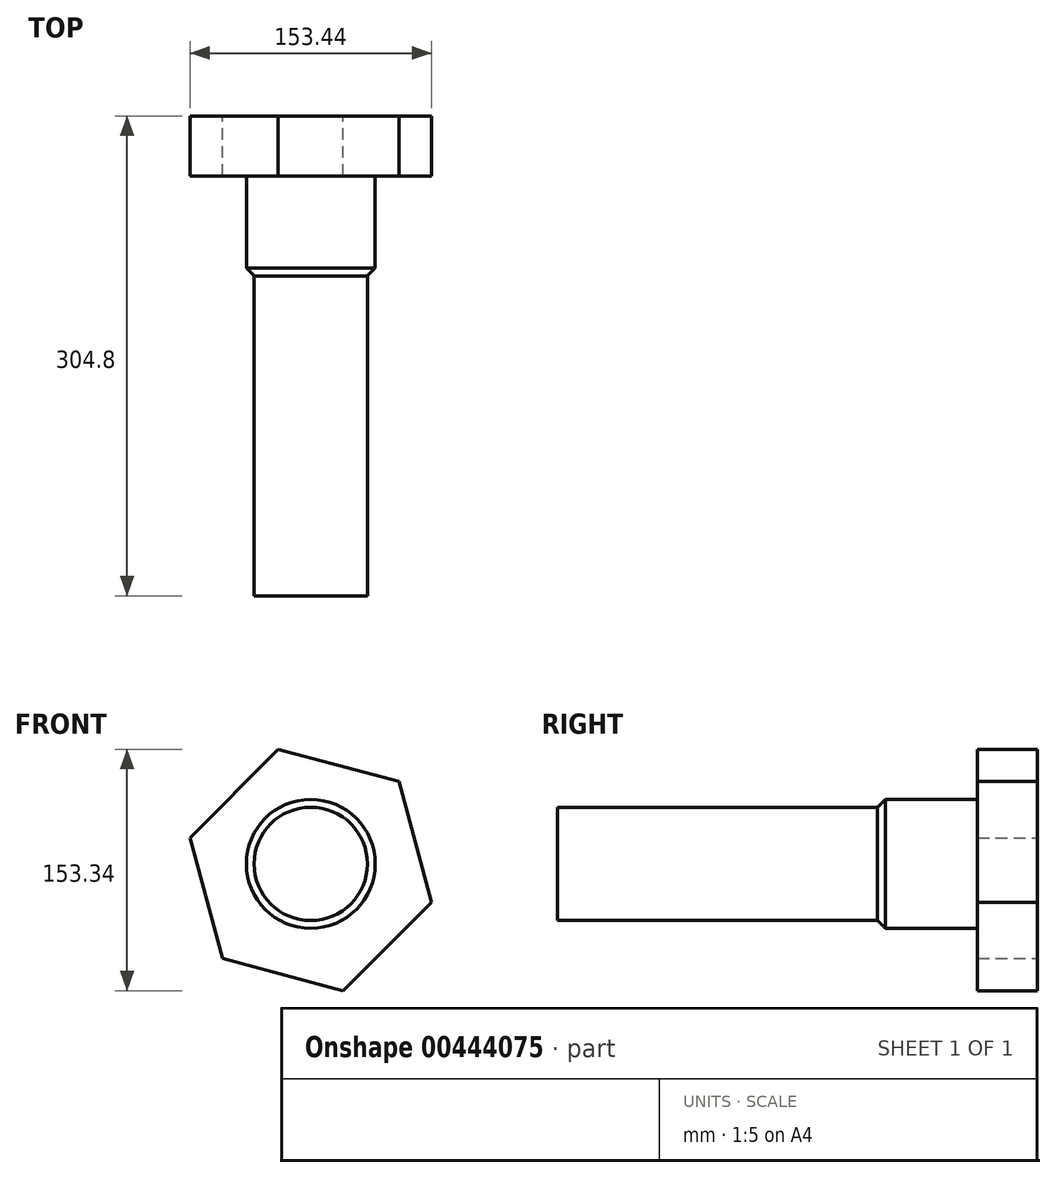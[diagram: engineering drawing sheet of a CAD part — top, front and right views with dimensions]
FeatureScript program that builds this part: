
annotation { "Feature Type Name" : "Feature", "Feature Type Description" : "" }
export const myFeature = defineFeature(function(context is Context, id is Id, definition is map)
    precondition{}
    {
        {
            var Q0;
            Q0=qCreatedBy(makeId("Front.planeOp"),FACE);
            var sketch = newSketch(context, id + "F0", { "sketchPlane" : qUnion([Q0])});
            skCircle(sketch, "E0.cCircle", {"center": v(0, -3.86) * mm, "radius": 68.77 * mm, "construction": true});
            skLineSegment(sketch, "E0.0", {"start": v(56.08, 52.35) * mm, "end": v(76.72, -24.32) * mm});
            skLineSegment(sketch, "E0.1", {"start": v(76.72, -24.32) * mm, "end": v(20.64, -80.53) * mm});
            skLineSegment(sketch, "E0.2", {"start": v(20.64, -80.53) * mm, "end": v(-56.08, -60.07) * mm});
            skLineSegment(sketch, "E0.3", {"start": v(-56.08, -60.07) * mm, "end": v(-76.72, 16.6) * mm});
            skLineSegment(sketch, "E0.4", {"start": v(-76.72, 16.6) * mm, "end": v(-20.64, 72.81) * mm});
            skLineSegment(sketch, "E0.5", {"start": v(-20.64, 72.81) * mm, "end": v(56.08, 52.35) * mm});
            skPoint(sketch, "E0.0.midPoint", {"position": v(66.4, 14.01) * mm});
            skSolve(sketch);
        }
        {
            var Q0;
            Q0 = qSketchRegion(id + "F0", true);
            extrude(context, id + "F1", {"entities" : qUnion([Q0]), "depth" : 38.1 * mm});
        }
        {
            var Q0;
            Q0=makeQuery(id+"F1.opExtrude","CAP_FACE",FACE,{"disambiguationData":[OSD([sQuery(id+"F0.wireOp",EDGE,"E0.0"),sQuery(id+"F0.wireOp",EDGE,"E0.1"),sQuery(id+"F0.wireOp",EDGE,"E0.2"),sQuery(id+"F0.wireOp",EDGE,"E0.3"),sQuery(id+"F0.wireOp",EDGE,"E0.4"),sQuery(id+"F0.wireOp",EDGE,"E0.5")])],"isStart":false});
            var sketch = newSketch(context, id + "F2", { "sketchPlane" : qUnion([Q0])});
            skCircle(sketch, "E1", {"center": v(0, 0) * mm, "radius": 40.93 * mm});
            skSolve(sketch);
        }
        {
            var Q0;
            Q0 = qSketchRegion(id + "F2", true);
            extrude(context, id + "F3", {"entities" : qUnion([Q0]), "operationType" : NewBodyOperationType.ADD, "depth" : 63.5 * mm});
        }
        {
            var Q0;
            Q0=makeQuery(id+"F3.opExtrude","CAP_EDGE",EDGE,{"disambiguationData":[OSD([sQuery(id+"F2.wireOp",EDGE,"E1")])],"isStart":false});
            chamfer(context, id + "F4", {"entities" : qUnion([Q0]), "width" : 5.08 * mm, "tangentPropagation" : true});
        }
        {
            var Q0;
            Q0=makeQuery(id+"F3.opExtrude","CAP_FACE",FACE,{"disambiguationData":[OSD([sQuery(id+"F2.wireOp",EDGE,"E1")])],"isStart":false});
            var sketch = newSketch(context, id + "F5", { "sketchPlane" : qUnion([Q0])});
            skCircle(sketch, "E2", {"center": v(0, 0) * mm, "radius": 35.98 * mm});
            skSolve(sketch);
        }
        {
            var Q0;
            Q0 = qSketchRegion(id + "F5", true);
            extrude(context, id + "F6", {"entities" : qUnion([Q0]), "operationType" : NewBodyOperationType.ADD, "depth" : 203.2 * mm});
        }
    });
